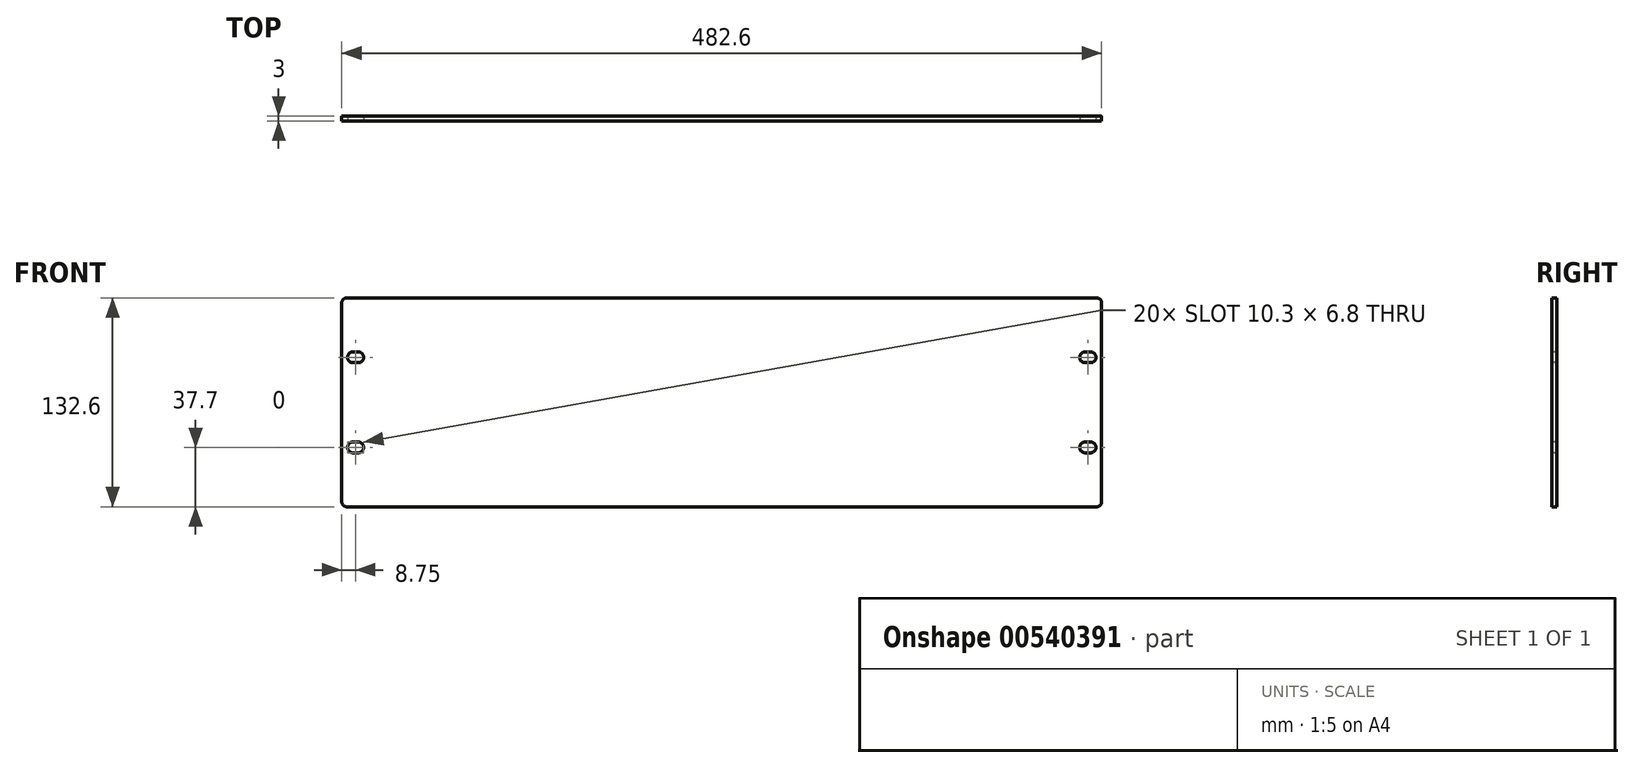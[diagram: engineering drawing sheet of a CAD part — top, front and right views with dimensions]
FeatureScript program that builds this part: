
annotation { "Feature Type Name" : "Feature", "Feature Type Description" : "" }
export const myFeature = defineFeature(function(context is Context, id is Id, definition is map)
    precondition{}
    {
        {
            var Q0;
            Q0=qCreatedBy(makeId("Front.planeOp"),FACE);
            var sketch = newSketch(context, id + "F0", { "sketchPlane" : qUnion([Q0])});
            skLineSegment(sketch, "E0.bottom", {"start": v(241.3, -66.3) * mm, "end": v(-241.3, -66.3) * mm});
            skLineSegment(sketch, "E0.top", {"start": v(241.3, 66.3) * mm, "end": v(-241.3, 66.3) * mm});
            skLineSegment(sketch, "E0.left", {"start": v(241.3, -66.3) * mm, "end": v(241.3, 66.3) * mm});
            skLineSegment(sketch, "E0.right", {"start": v(-241.3, -66.3) * mm, "end": v(-241.3, 66.3) * mm});
            skPoint(sketch, "E0.middle", {"position": v(0, 0) * mm});
            skSolve(sketch);
        }
        {
            var Q0;
            Q0=makeQuery(id+"F0.imprint","IMPRINT",FACE,{"disambiguationData":[TD([[makeQuery(id+"F0.imprint","IMPRINT",EDGE,{"derivedFrom":sQuery(id+"F0.wireOp",EDGE,"E0.bottom")}),-1.0]])]});
            extrude(context, id + "F1", {"entities" : qUnion([Q0]), "oppositeDirection" : true, "depth" : 3 * mm, "offsetDistance" : 25 * mm});
        }
        {
            var Q0;
            Q0=makeQuery(id+"F1.opExtrude","SWEPT_EDGE",EDGE,{"disambiguationData":[OSD([sQuery(id+"F0.wireOp",EDGE,"E0.top"),sQuery(id+"F0.wireOp",EDGE,"E0.right")])]});
            var Q1;
            Q1=makeQuery(id+"F1.opExtrude","SWEPT_EDGE",EDGE,{"disambiguationData":[OSD([sQuery(id+"F0.wireOp",EDGE,"E0.top"),sQuery(id+"F0.wireOp",EDGE,"E0.left")])]});
            var Q2;
            Q2=makeQuery(id+"F1.opExtrude","SWEPT_EDGE",EDGE,{"disambiguationData":[OSD([sQuery(id+"F0.wireOp",EDGE,"E0.bottom"),sQuery(id+"F0.wireOp",EDGE,"E0.left")])]});
            var Q3;
            Q3=makeQuery(id+"F1.opExtrude","SWEPT_EDGE",EDGE,{"disambiguationData":[OSD([sQuery(id+"F0.wireOp",EDGE,"E0.bottom"),sQuery(id+"F0.wireOp",EDGE,"E0.right")])]});
            fillet(context, id + "F2", {"entities" : qUnion([Q0, Q1, Q2, Q3]), "radius" : 3 * mm, "tangentPropagation" : true, "allowEdgeOverflow" : false});
        }
        {
            var Q0;
            Q0=qCreatedBy(makeId("Front.planeOp"),FACE);
            var sketch = newSketch(context, id + "F3", { "sketchPlane" : qUnion([Q0])});
            skArc(sketch, "E1", {"start": v(-230.8, 25.2) * mm, "mid": v(-227.4, 28.6) * mm, "end": v(-230.8, 32) * mm});
            skArc(sketch, "E2", {"start": v(-234.3, 32) * mm, "mid": v(-237.7, 28.6) * mm, "end": v(-234.3, 25.2) * mm});
            skLineSegment(sketch, "E3", {"start": v(-234.3, 32) * mm, "end": v(-230.8, 32) * mm});
            skLineSegment(sketch, "E4", {"start": v(-234.3, 25.2) * mm, "end": v(-230.8, 25.2) * mm});
            skArc(sketch, "E5.MirrorCS", {"start": v(230.8, 25.2) * mm, "mid": v(227.4, 28.6) * mm, "end": v(230.8, 32) * mm});
            skLineSegment(sketch, "E6.MirrorCS", {"start": v(234.3, 32) * mm, "end": v(230.8, 32) * mm});
            skArc(sketch, "E7.MirrorCS", {"start": v(234.3, 32) * mm, "mid": v(237.7, 28.6) * mm, "end": v(234.3, 25.2) * mm});
            skLineSegment(sketch, "E8.MirrorCS", {"start": v(234.3, 25.2) * mm, "end": v(230.8, 25.2) * mm});
            skArc(sketch, "E9.MirrorCS", {"start": v(234.3, -32) * mm, "mid": v(237.7, -28.6) * mm, "end": v(234.3, -25.2) * mm});
            skArc(sketch, "E10.MirrorCS", {"start": v(230.8, -25.2) * mm, "mid": v(227.4, -28.6) * mm, "end": v(230.8, -32) * mm});
            skLineSegment(sketch, "E11.MirrorCS", {"start": v(234.3, -25.2) * mm, "end": v(230.8, -25.2) * mm});
            skLineSegment(sketch, "E12.MirrorCS", {"start": v(234.3, -32) * mm, "end": v(230.8, -32) * mm});
            skArc(sketch, "E13.MirrorCS", {"start": v(-230.8, -25.2) * mm, "mid": v(-227.4, -28.6) * mm, "end": v(-230.8, -32) * mm});
            skLineSegment(sketch, "E14.MirrorCS", {"start": v(-234.3, -32) * mm, "end": v(-230.8, -32) * mm});
            skArc(sketch, "E15.MirrorCS", {"start": v(-234.3, -32) * mm, "mid": v(-237.7, -28.6) * mm, "end": v(-234.3, -25.2) * mm});
            skLineSegment(sketch, "E16.MirrorCS", {"start": v(-234.3, -25.2) * mm, "end": v(-230.8, -25.2) * mm});
            skSolve(sketch);
        }
        {
            var Q0;
            Q0=qSketchRegion(id+"F3",true);
            extrude(context, id + "F4", {"entities" : qUnion([Q0]), "operationType" : NewBodyOperationType.REMOVE, "endBound" : BoundingType.UP_TO_NEXT, "oppositeDirection" : true, "depth" : 25 * mm, "offsetDistance" : 25 * mm});
        }
    });
